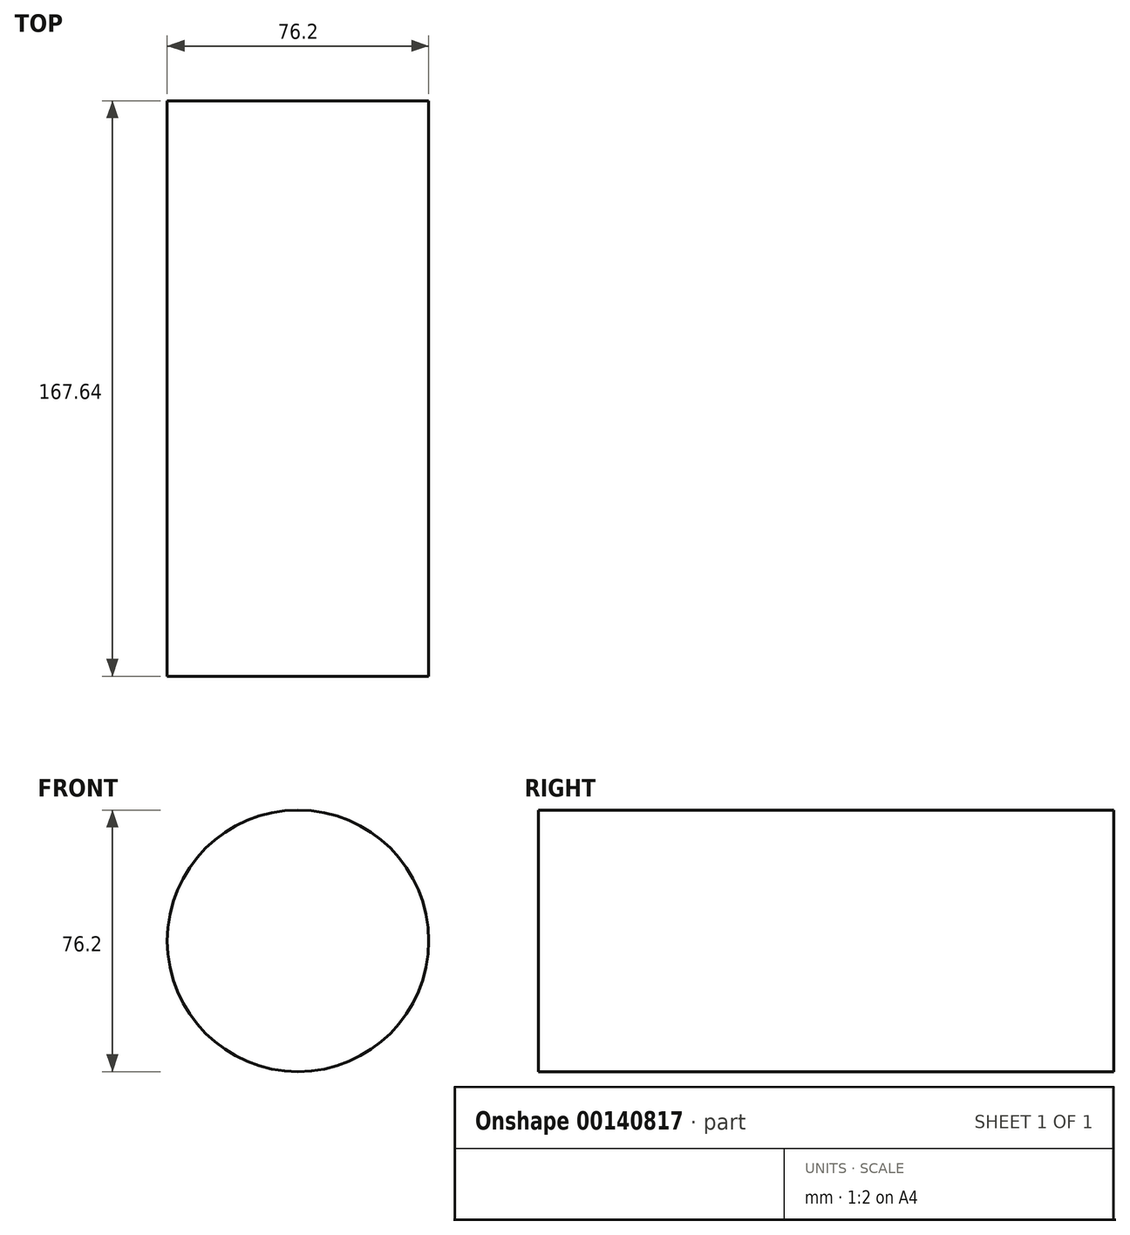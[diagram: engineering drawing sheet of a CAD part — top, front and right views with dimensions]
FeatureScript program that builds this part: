
annotation { "Feature Type Name" : "Feature", "Feature Type Description" : "" }
export const myFeature = defineFeature(function(context is Context, id is Id, definition is map)
    precondition{}
    {
        {
            var Q0;
            Q0=qCreatedBy(makeId("Front.planeOp"),FACE);
            var sketch = newSketch(context, id + "F0", { "sketchPlane" : qUnion([Q0])});
            skCircle(sketch, "E0", {"center": v(0, 0) * mm, "radius": 38.1 * mm});
            skSolve(sketch);
        }
        {
            var Q0;
            Q0=makeQuery(id+"F0.imprint","IMPRINT",FACE,{"disambiguationData":[TD([[makeQuery(id+"F0.imprint","IMPRINT",EDGE,{"derivedFrom":sQuery(id+"F0.wireOp",EDGE,"E0")}),1.0]])]});
            extrude(context, id + "F1", {"entities" : qUnion([Q0]), "endBound" : BoundingType.SYMMETRIC, "depth" : 167.64 * mm});
        }
    });
